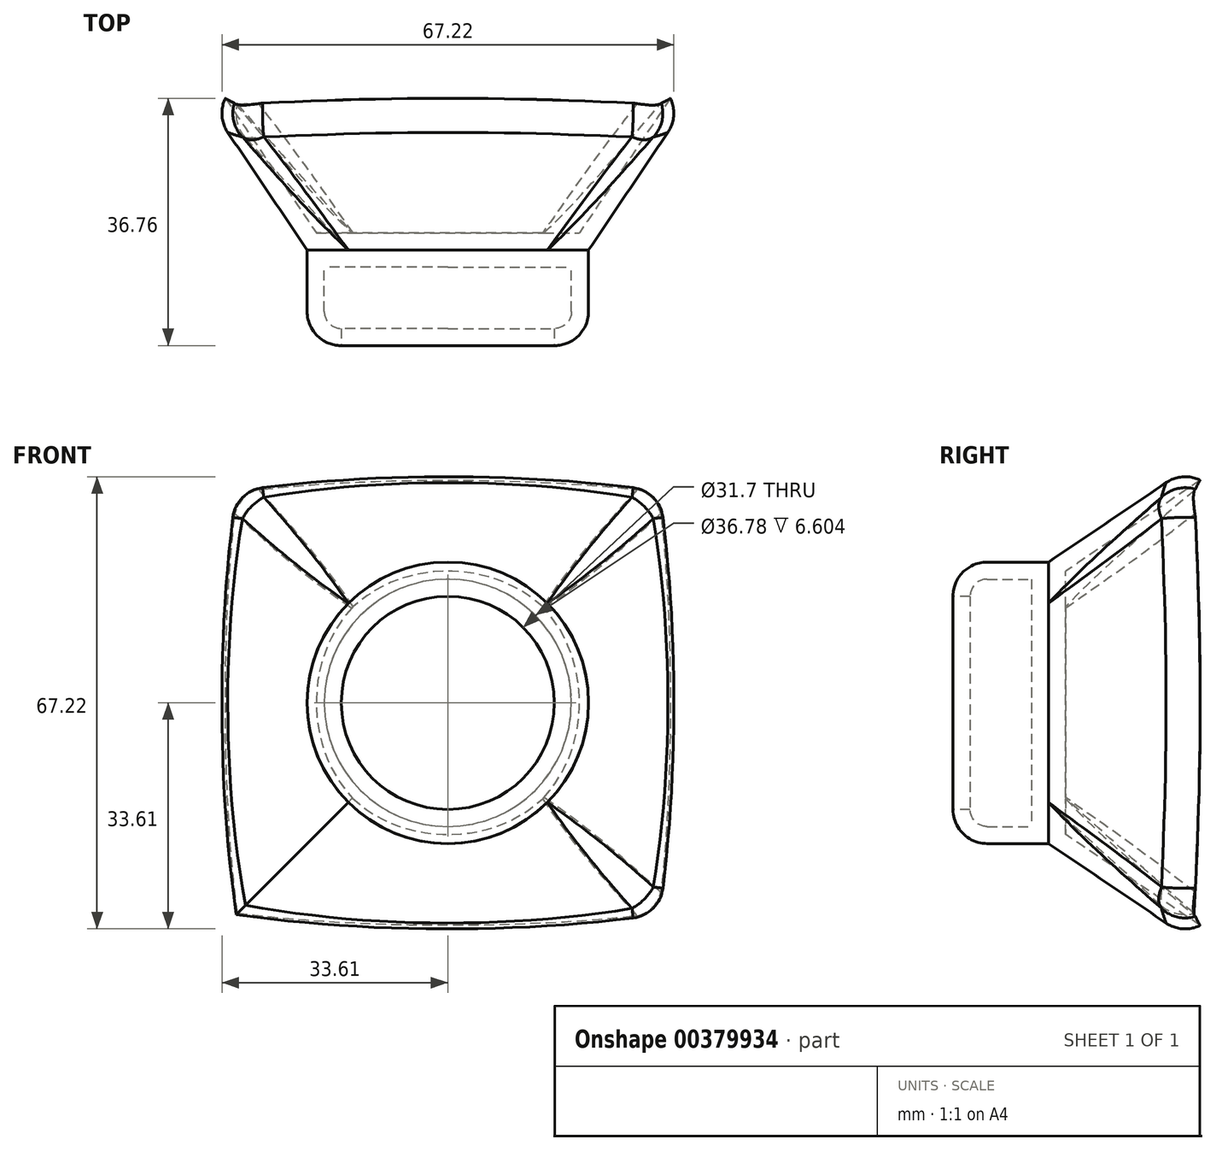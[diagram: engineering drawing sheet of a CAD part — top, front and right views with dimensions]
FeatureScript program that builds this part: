
annotation { "Feature Type Name" : "Feature", "Feature Type Description" : "" }
export const myFeature = defineFeature(function(context is Context, id is Id, definition is map)
    precondition{}
    {
        {
            var Q0;
            Q0=qCreatedBy(makeId("Front.planeOp"),FACE);
            var sketch = newSketch(context, id + "F0", { "sketchPlane" : qUnion([Q0])});
            skCircle(sketch, "E0", {"center": v(0, 0) * mm, "radius": 20.93 * mm});
            skSolve(sketch);
        }
        {
            var Q0;
            Q0=makeQuery(id+"F0.imprint","IMPRINT",FACE,{"disambiguationData":[TD([[makeQuery(id+"F0.imprint","IMPRINT",EDGE,{"derivedFrom":sQuery(id+"F0.wireOp",EDGE,"E0")}),1.0]])]});
            extrude(context, id + "F1", {"entities" : qUnion([Q0]), "depth" : 39.62 * mm});
        }
        {
            var Q0;
            Q0=makeQuery(id+"F1.opExtrude","CAP_FACE",FACE,{"disambiguationData":[OSD([sQuery(id+"F0.wireOp",EDGE,"E0")])],"isStart":true});
            extrude(context, id + "F2", {"entities" : qUnion([Q0]), "operationType" : NewBodyOperationType.REMOVE, "oppositeDirection" : true, "depth" : 25.4 * mm});
        }
        {
            var Q0;
            Q0=qCreatedBy(makeId("Front.planeOp"),FACE);
            var sketch = newSketch(context, id + "F3", { "sketchPlane" : qUnion([Q0])});
            skLineSegment(sketch, "E1.bottom", {"start": v(-38.1, 38.1) * mm, "end": v(38.1, 38.1) * mm});
            skLineSegment(sketch, "E1.top", {"start": v(-38.1, -38.1) * mm, "end": v(38.1, -38.1) * mm});
            skLineSegment(sketch, "E1.left", {"start": v(-38.1, 38.1) * mm, "end": v(-38.1, -38.1) * mm});
            skLineSegment(sketch, "E1.right", {"start": v(38.1, 38.1) * mm, "end": v(38.1, -38.1) * mm});
            skPoint(sketch, "E1.middle", {"position": v(0, 0) * mm});
            skSolve(sketch);
        }
        {
            var Q0;
            Q0=makeQuery(id+"F3.imprint","IMPRINT",FACE,{"disambiguationData":[TD([[makeQuery(id+"F3.imprint","IMPRINT",EDGE,{"derivedFrom":sQuery(id+"F3.wireOp",EDGE,"E1.bottom")}),-1.0]])]});
            var Q1;
            Q1=makeQuery(id+"F2.boolean.opBoolean","COPY",FACE,{"derivedFrom":makeQuery(id+"F2.opExtrude","CAP_FACE",FACE,{"disambiguationData":[OSD([sQuery(id+"F0.wireOp",EDGE,"E0")])],"isStart":false})});
            loft(context, id + "F4", {"sheetProfilesArray" : [{ "sheetProfileEntities" : qUnion([Q0]) }, { "sheetProfileEntities" : qUnion([Q1]) }]});
        }
        {
            var Q0;
            Q0=makeQuery(id+"F4.opLoft","CAP_FACE",FACE,{"disambiguationData":[OSD([makeQuery(id+"F3.imprint","IMPRINT",FACE,{"disambiguationData":[TD([[makeQuery(id+"F3.imprint","IMPRINT",EDGE,{"derivedFrom":sQuery(id+"F3.wireOp",EDGE,"E1.bottom")}),-1.0]])]})])],"isStart":true});
            shell(context, id + "F5", {"entities" : qUnion([Q0]), "thickness" : 2.54 * mm});
        }
        {
            var Q0;
            Q0=makeQuery(id+"F4.opLoft","MID_CAP_EDGE",EDGE,{"disambiguationData":[OSD([sQuery(id+"F3.wireOp",EDGE,"E1.top"),sQuery(id+"F3.wireOp",EDGE,"E1.left"),sQuery(id+"F3.wireOp",EDGE,"E1.right")])],"capPos":0.0});
            var Q1;
            Q1=makeQuery(id+"F4.opLoft","MID_CAP_EDGE",EDGE,{"disambiguationData":[OSD([sQuery(id+"F3.wireOp",EDGE,"E1.bottom"),sQuery(id+"F3.wireOp",EDGE,"E1.top"),sQuery(id+"F3.wireOp",EDGE,"E1.right")])],"capPos":0.0});
            var Q2;
            Q2=makeQuery(id+"F4.opLoft","MID_CAP_EDGE",EDGE,{"disambiguationData":[OSD([sQuery(id+"F3.wireOp",EDGE,"E1.bottom"),sQuery(id+"F3.wireOp",EDGE,"E1.top"),sQuery(id+"F3.wireOp",EDGE,"E1.left")])],"capPos":0.0});
            var Q3;
            Q3=makeQuery(id+"F4.opLoft","MID_CAP_EDGE",EDGE,{"disambiguationData":[OSD([sQuery(id+"F3.wireOp",EDGE,"E1.bottom"),sQuery(id+"F3.wireOp",EDGE,"E1.left"),sQuery(id+"F3.wireOp",EDGE,"E1.right")])],"capPos":0.0});
            var Q4;
            Q4=makeQuery(id+"F1.opExtrude","CAP_EDGE",EDGE,{"disambiguationData":[OSD([sQuery(id+"F0.wireOp",EDGE,"E0")])],"isStart":false});
            fillet(context, id + "F6", {"entities" : qUnion([Q0, Q1, Q2, Q3, Q4]), "radius" : 5.08 * mm, "tangentPropagation" : true, "allowEdgeOverflow" : false});
        }
        {
            var Q0;
            Q0=makeQuery(id+"F4.opLoft","SWEPT_EDGE",EDGE,{"disambiguationData":[OSD([sQuery(id+"F0.wireOp",EDGE,"E0"),sQuery(id+"F3.wireOp",EDGE,"E1.bottom"),sQuery(id+"F3.wireOp",EDGE,"E1.top"),sQuery(id+"F3.wireOp",EDGE,"E1.right")])]});
            var Q1;
            Q1=makeQuery(id+"F4.opLoft","SWEPT_EDGE",EDGE,{"disambiguationData":[OSD([sQuery(id+"F0.wireOp",EDGE,"E0"),sQuery(id+"F3.wireOp",EDGE,"E1.top"),sQuery(id+"F3.wireOp",EDGE,"E1.left"),sQuery(id+"F3.wireOp",EDGE,"E1.right")])]});
            var Q2;
            Q2=makeQuery(id+"F4.opLoft","SWEPT_EDGE",EDGE,{"disambiguationData":[OSD([sQuery(id+"F0.wireOp",EDGE,"E0"),sQuery(id+"F3.wireOp",EDGE,"E1.bottom"),sQuery(id+"F3.wireOp",EDGE,"E1.top"),sQuery(id+"F3.wireOp",EDGE,"E1.left")])]});
            var Q3;
            Q3=makeQuery(id+"F4.opLoft","SWEPT_EDGE",EDGE,{"disambiguationData":[OSD([sQuery(id+"F3.wireOp",EDGE,"E1.bottom"),sQuery(id+"F3.wireOp",EDGE,"E1.left")])]});
            var Q4;
            Q4=makeQuery(id+"F5.opShell","OFFSET_EDGE",EDGE,{"disambiguationData":[OSD([sQuery(id+"F0.wireOp",EDGE,"E0"),sQuery(id+"F3.wireOp",EDGE,"E1.bottom"),sQuery(id+"F3.wireOp",EDGE,"E1.top"),sQuery(id+"F3.wireOp",EDGE,"E1.right")])]});
            var Q5;
            {var subQ0=sQuery(id+"F3.wireOp",EDGE,"E1.right");var subQ1=sQuery(id+"F3.wireOp",EDGE,"E1.left");var subQ2=sQuery(id+"F3.wireOp",EDGE,"E1.top");var subQ3=sQuery(id+"F0.wireOp",EDGE,"E0");Q5=makeQuery(id+"F5.opShell","OFFSET_EDGE",EDGE,{"disambiguationData":[OSD([subQ3,subQ2,subQ1,subQ0]),TDD([makeQuery(id+"F4.opLoft","SWEPT_EDGE",EDGE,{"disambiguationData":[OSD([subQ3,subQ2,subQ1,subQ0])]})])]});}
            var Q6;
            {var subQ0=sQuery(id+"F3.wireOp",EDGE,"E1.left");var subQ1=sQuery(id+"F3.wireOp",EDGE,"E1.top");var subQ2=sQuery(id+"F3.wireOp",EDGE,"E1.bottom");var subQ3=sQuery(id+"F0.wireOp",EDGE,"E0");Q6=makeQuery(id+"F5.opShell","OFFSET_EDGE",EDGE,{"disambiguationData":[OSD([subQ3,subQ2,subQ1,subQ0]),TDD([makeQuery(id+"F4.opLoft","SWEPT_EDGE",EDGE,{"disambiguationData":[OSD([subQ3,subQ2,subQ1,subQ0])]})])]});}
            var Q7;
            Q7=makeQuery(id+"F5.opShell","OFFSET_EDGE",EDGE,{"disambiguationData":[OSD([sQuery(id+"F3.wireOp",EDGE,"E1.bottom"),sQuery(id+"F3.wireOp",EDGE,"E1.left")])]});
            fillet(context, id + "F7", {"entities" : qUnion([Q0, Q1, Q2, Q3, Q4, Q5, Q6, Q7]), "radius" : 5.08 * mm, "tangentPropagation" : true, "allowEdgeOverflow" : false});
        }
        {
            var Q0;
            Q0=makeQuery(id+"F1.opExtrude","CAP_FACE",FACE,{"disambiguationData":[OSD([sQuery(id+"F0.wireOp",EDGE,"E0")])],"isStart":false});
            shell(context, id + "F8", {"entities" : qUnion([Q0]), "thickness" : 2.54 * mm});
        }
    });
